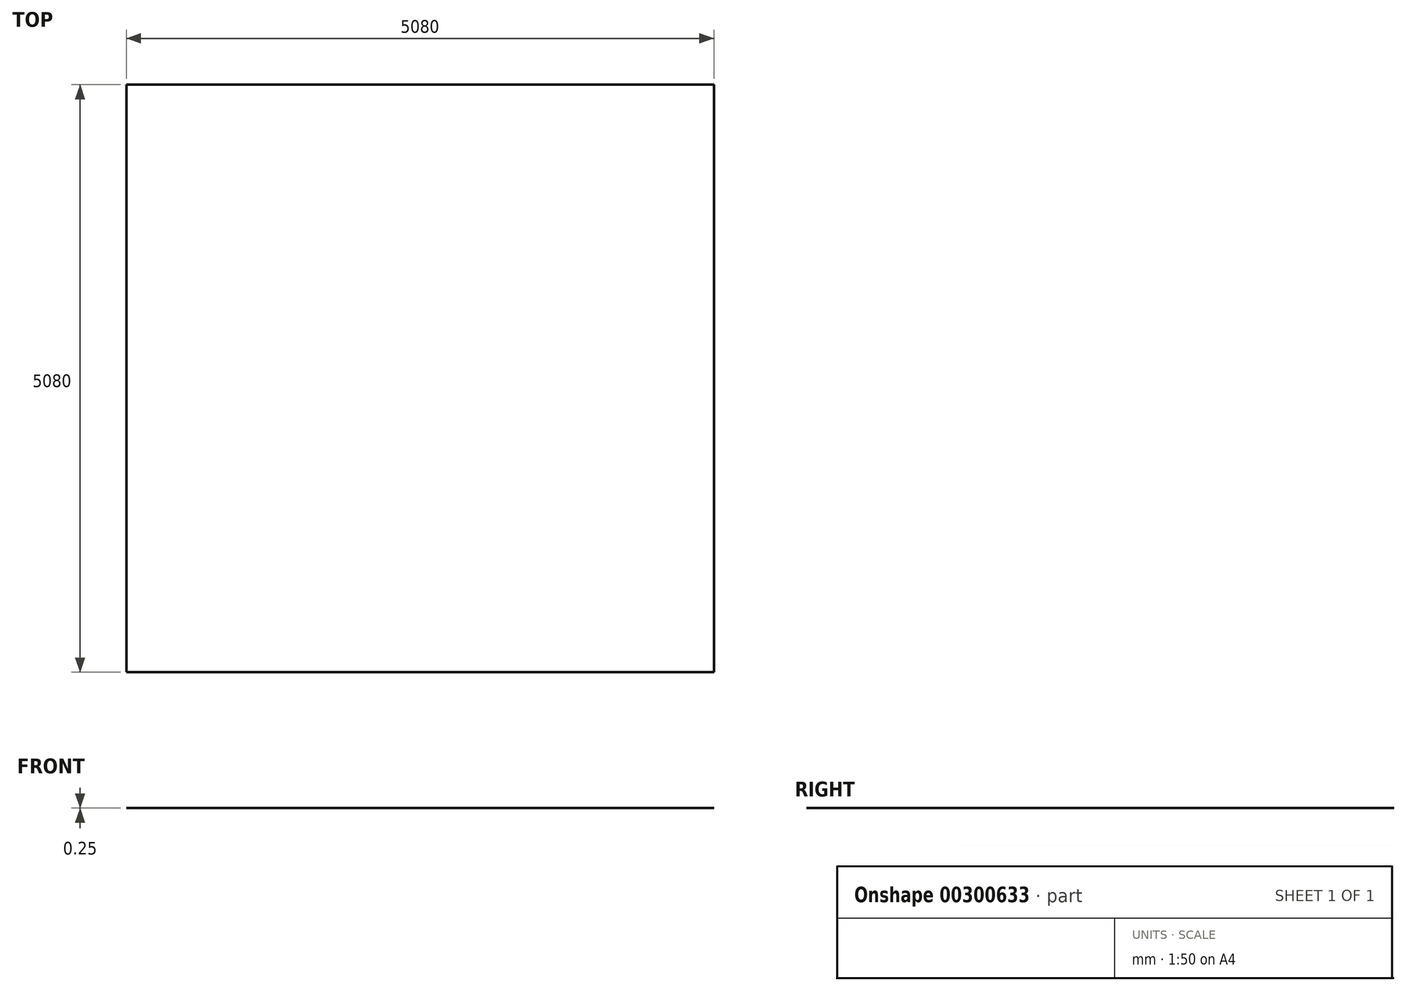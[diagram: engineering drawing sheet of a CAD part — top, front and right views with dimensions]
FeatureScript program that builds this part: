
annotation { "Feature Type Name" : "Feature", "Feature Type Description" : "" }
export const myFeature = defineFeature(function(context is Context, id is Id, definition is map)
    precondition{}
    {
        {
            var Q0;
            Q0=qCreatedBy(makeId("Top.planeOp"),FACE);
            var sketch = newSketch(context, id + "F0", { "sketchPlane" : qUnion([Q0])});
            skLineSegment(sketch, "E0.bottom", {"start": v(2540, -2540) * mm, "end": v(-2540, -2540) * mm});
            skLineSegment(sketch, "E0.top", {"start": v(2540, 2540) * mm, "end": v(-2540, 2540) * mm});
            skLineSegment(sketch, "E0.left", {"start": v(2540, -2540) * mm, "end": v(2540, 2540) * mm});
            skLineSegment(sketch, "E0.right", {"start": v(-2540, -2540) * mm, "end": v(-2540, 2540) * mm});
            skPoint(sketch, "E0.middle", {"position": v(0, 0) * mm});
            skSolve(sketch);
        }
        {
            var Q0;
            Q0 = qSketchRegion(id + "F0", true);
            extrude(context, id + "F1", {"entities" : qUnion([Q0]), "depth" : 0.25 * mm});
        }
    });
